# Revit family: KLV52
name_source: partatom
category: Lighting Fixtures
units: mm (PartAtom-declared; Revit-internal decimal feet)

## family parameters
Always vertical = No
Cut with Voids When Loaded = No
Light Source = Yes
OmniClass Number = 23.80.70.14.21
OmniClass Title = Street and Roadway Lighting
Part Type = Normal
Room Calculation Point = No
Round Connector Dimension = Use Diameter
Shared = No
Work Plane-Based = Yes

## types (1)
- KLV52
    Apparent Load = 0 VA
    Assembly Code = D5020200
    Color Filter = 16777215
    Default Elevation = 48"
    Description = Site/Roadway Luminaire
    Dimming Lamp Color Temperature Shift = <None>
    Emit Shape Visible in Rendering = No
    Emit from Circle Diameter = 5"
    Finish = All colors shall be a Super TGIC powder coat paint. Optional white (WH) and custom colors available.
    Glass Material = Glass-Clear
    Height = 22"
    Housing Material = Metal-Aluminum Alloy
    Lamp = LED
    Load Classification = Lighting
    Manufacturer = Kim Lighting
    MasterFormat Title = Parking Lighting, Roadway Lighting, Site Lighting
    Model = Bell
    Mount Height = 45 1/2"
    Number of Poles = 1
    OmniClass Number = 23-80 70 14 21
    OmniClass Title = Street and Roadway Lighting
    Photometric Notes = More IES files download on Photometric Web Link
    Photometric Web File = an52-9l3k.ies
    Pole Height = 29"
    Power Factor = 0.9
    Series = Bell Accent/Path/Wall Lighting
    Tilt Angle = -90.00°
    Type Comments = Lighting Fixture
    URL = https://www.currentlighting.com
    Voltage = 120 V
    Wattage Comments = 12W

## geometry (parser evidence)
native form markers: Blend x12, Sweep x1
no freeform markers — native parametric forms only
